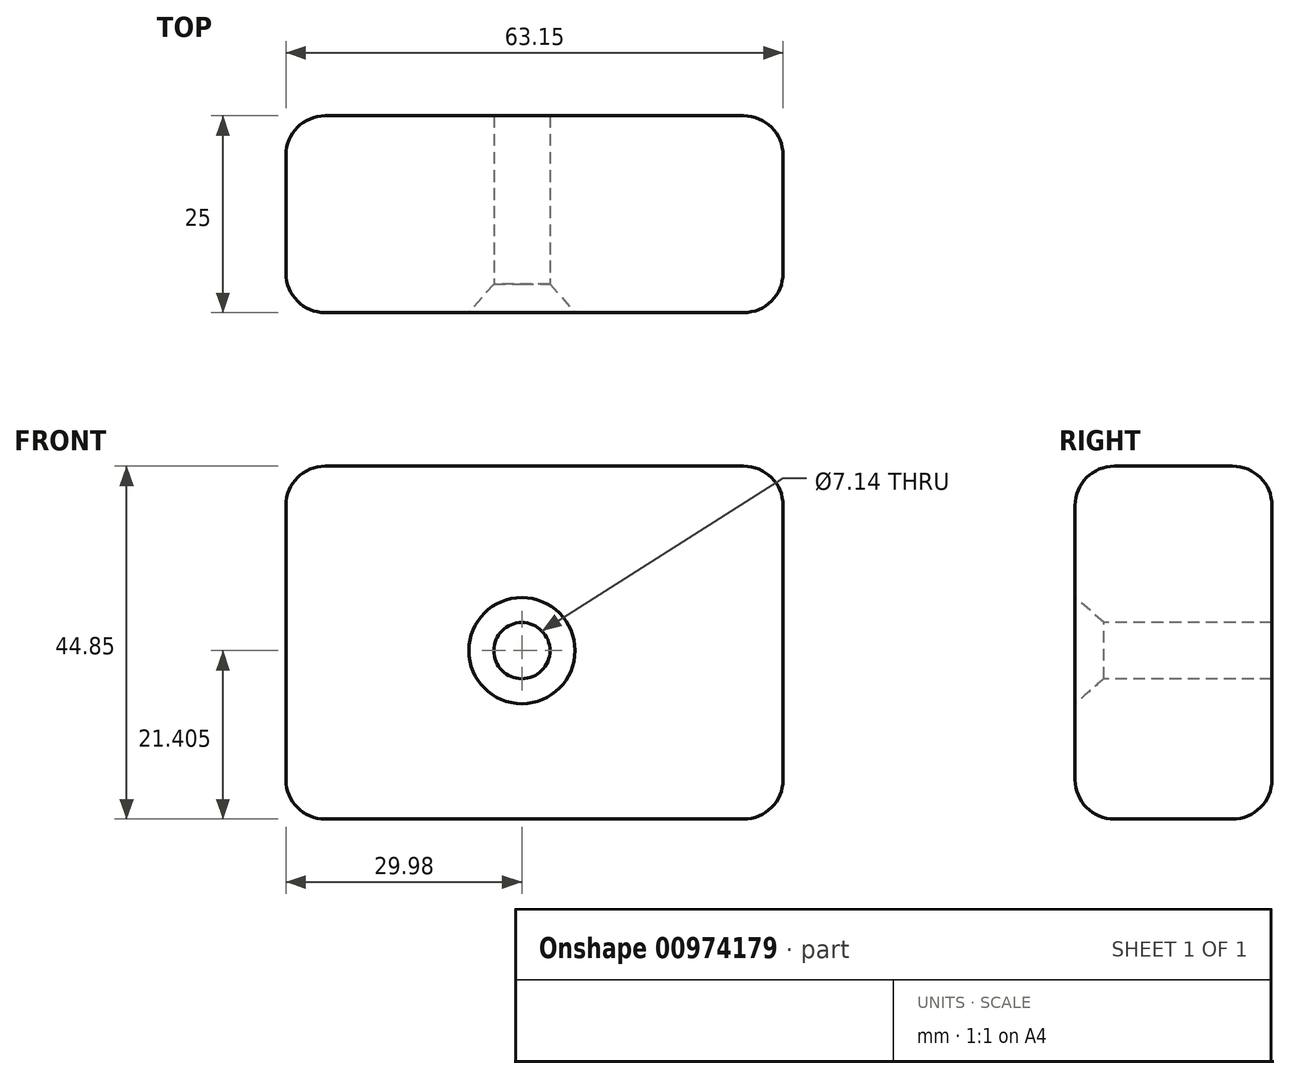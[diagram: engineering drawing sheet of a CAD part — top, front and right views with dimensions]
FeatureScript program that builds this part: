
annotation { "Feature Type Name" : "Feature", "Feature Type Description" : "" }
export const myFeature = defineFeature(function(context is Context, id is Id, definition is map)
    precondition{}
    {
        {
            var Q0;
            Q0=qCreatedBy(makeId("Front.planeOp"),FACE);
            var sketch = newSketch(context, id + "F0", { "sketchPlane" : qUnion([Q0])});
            skLineSegment(sketch, "E0.bottom", {"start": v(0, 0) * mm, "end": v(63.15, 0) * mm});
            skLineSegment(sketch, "E0.top", {"start": v(0, -44.85) * mm, "end": v(63.15, -44.85) * mm});
            skLineSegment(sketch, "E0.left", {"start": v(0, 0) * mm, "end": v(0, -44.85) * mm});
            skLineSegment(sketch, "E0.right", {"start": v(63.15, 0) * mm, "end": v(63.15, -44.85) * mm});
            skSolve(sketch);
        }
        {
            var Q0;
            Q0 = qSketchRegion(id + "F0", true);
            extrude(context, id + "F1", {"entities" : qUnion([Q0]), "depth" : 25 * mm, "offsetDistance" : 25 * mm});
        }
        {
            var Q0;
            Q0=makeQuery(id+"F1.opExtrude","CAP_FACE",FACE,{"disambiguationData":[OSD([sQuery(id+"F0.wireOp",EDGE,"E0.bottom"),sQuery(id+"F0.wireOp",EDGE,"E0.top"),sQuery(id+"F0.wireOp",EDGE,"E0.left"),sQuery(id+"F0.wireOp",EDGE,"E0.right")])],"isStart":false});
            var sketch = newSketch(context, id + "F2", { "sketchPlane" : qUnion([Q0])});
            skPoint(sketch, "E1", {"position": v(29.98, -23.45) * mm});
            skSolve(sketch);
        }
        {
            var Q0;
            Q0=sQuery(id+"F2.wireOp",VERTEX,"E1");
            var Q1;
            Q1=makeQuery(id+"F1.opExtrude","SWEPT_BODY",BODY,{"disambiguationData":[OSD([sQuery(id+"F0.wireOp",EDGE,"E0.bottom"),sQuery(id+"F0.wireOp",EDGE,"E0.top"),sQuery(id+"F0.wireOp",EDGE,"E0.left"),sQuery(id+"F0.wireOp",EDGE,"E0.right")])]});
            hole(context, id + "F3", {"style" : HoleStyle.C_SINK, "endStyle" : HoleEndStyle.THROUGH, "standardTappedOrClearance" : lookupTablePath({ "fit" : "Normal (ASME)", "standard" : "ANSI", "size" : "1/4", "type" : "Clearance" }), "standardBlindInLast" : lookupTablePath({ "fit" : "Normal", "standard" : "ANSI", "engagement" : "75%", "pitch" : "20 tpi", "size" : "1/4", "type" : "Clearance & tapped" }), "holeDiameter" : 7.14 * mm, "cSinkDiameter" : 13.5 * mm, "cSinkAngle" : 82 * degree, "majorDiameter" : 5 * mm, "isTappedThrough" : true, "tappedDepth" : 12 * mm, "tapClearance" : 3, "locations" : qUnion([Q0]), "scope" : qUnion([Q1])});
        }
        {
            var Q0;
            Q0=makeQuery(id+"F1.opExtrude","SWEPT_FACE",FACE,{"disambiguationData":[OSD([sQuery(id+"F0.wireOp",EDGE,"E0.bottom")])]});
            var Q1;
            Q1=makeQuery(id+"F1.opExtrude","SWEPT_FACE",FACE,{"disambiguationData":[OSD([sQuery(id+"F0.wireOp",EDGE,"E0.left")])]});
            var Q2;
            Q2=makeQuery(id+"F1.opExtrude","SWEPT_FACE",FACE,{"disambiguationData":[OSD([sQuery(id+"F0.wireOp",EDGE,"E0.top")])]});
            var Q3;
            Q3=makeQuery(id+"F1.opExtrude","SWEPT_FACE",FACE,{"disambiguationData":[OSD([sQuery(id+"F0.wireOp",EDGE,"E0.right")])]});
            fillet(context, id + "F4", {"entities" : qUnion([Q0, Q1, Q2, Q3]), "radius" : 5 * mm, "tangentPropagation" : true, "allowEdgeOverflow" : false});
        }
    });
